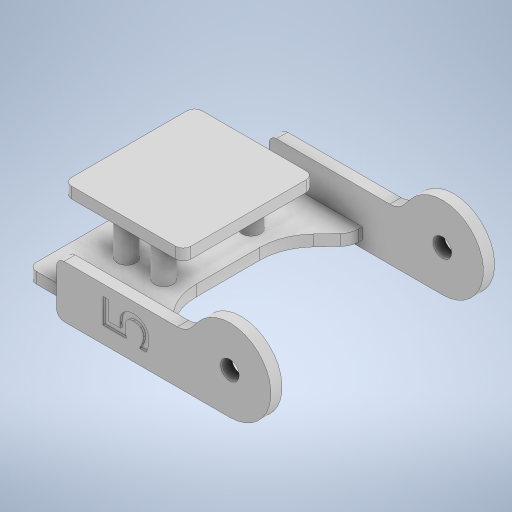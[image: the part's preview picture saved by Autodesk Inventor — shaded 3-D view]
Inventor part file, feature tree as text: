
AUTODESK INVENTOR PART (.ipt)
format: ipt  version: 2023 (Build 270158000, 158)  size: 394,752 bytes
history: native  units: mm
features: extrude x6, sketch x6, plane x4, other x1, mirror x1, fillet x1
ambient origin geometry x8: Origin, YZ Plane, XZ Plane, XY Plane, X Axis, Y Axis, Z Axis, Center Point
bodies: Body1 (feature_tree)
feature tree (19):
  other  "Sólido1"
  plane  "Plano de trabajo1"
  extrude  "Extrusión1"  Depth=22.0mm
  mirror  "Simetría1"
  plane  "Plano de trabajo2"
  extrude  "Extrusión2"  Depth=14.0mm
  plane  "Plano de trabajo3"
  extrude  "Extrusión3"  Depth=2.0mm
  extrude  "Extrusión4"  Depth=3.0mm TaperAngle=0.0deg
  fillet  "Empalme1"  [1 undecoded]
  extrude  "Extrusión5"  Depth=11.5mm
  plane  "Plano de trabajo4"
  extrude  "Extrusión6"  Depth=2.0mm
  sketch  "Boceto1"  dims[d0=27.0mm d1=22.0mm]
  sketch  "Boceto2"  dims[d3=5.0mm d4=14.0mm]
  sketch  "Boceto3"  dims[d5=57.5mm d6=2.0mm]
  sketch  "Boceto4"  dims[d7=5.0mm d8=3.0mm d9=0.0mm d10=-5.0mm]
  sketch  "Boceto5"  dims[d11=26.5mm d12=11.5mm]
  sketch  "Boceto6"  dims[d13=9.0mm d14=9.0mm d16=5.0mm d17=1.0mm d18=1.0mm d19=27.0mm d20=3.0mm d21=0.0mm d22=12.0mm d23=35.0mm d24=32.0mm d25=27.0mm d26=2.0mm d27=3.0mm d28=0.0mm d29=5.0mm d30=10.0mm d31=16.0mm d32=11.75mm d33=3.0mm d34=0.0mm d35=15.0mm d36=0.5mm d37=0.0mm d38=18.0mm d39=0.0mm d40=2.0mm]
note: 1 required parameter value undecoded (feature->parameter linkage not recoverable at this tier; creation-order binding heuristic only, values carry confidence <= 0.55)
